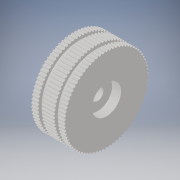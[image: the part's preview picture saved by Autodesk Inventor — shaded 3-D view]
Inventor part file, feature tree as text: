
AUTODESK INVENTOR PART (.ipt)
format: ipt  version: 2019 (Build 230136000, 136)  size: 681,984 bytes
history: native  units: in
note: dims shown in document units (in); Inventor stores cm internally (conversion verified against a paired STEP export)
features: sketch x7, extrude x6, revolve x1, projected_geometry x1
ambient origin geometry x8: Origin, YZ Plane, XZ Plane, XY Plane, X Axis, Y Axis, Z Axis, Center Point
bodies: Solid1 (feature_tree)
feature tree (15):
  extrude  "Extrusion1"  Depth=1.0in TaperAngle=0.0deg
  extrude  "Extrusion2"  Depth=0.27in TaperAngle=0.0deg
  extrude  "Extrusion3"  Depth=0.27in TaperAngle=0.0deg
  extrude  "Extrusion8"  Depth=0.3937in TaperAngle=0.0deg
  extrude  "Extrusion10"  Depth=1.0in TaperAngle=0.0deg
  extrude  "Extrusion11"  Depth=31.4961in TaperAngle=360.0deg
  revolve  "Revolution2"  [1 undecoded]
  sketch  "Sketch1"  dims[d3=0.35in d4=1.0in d5=0.0in]
  sketch  "Sketch2"  dims[d6=0.865in d7=0.27in d8=0.0in]
  sketch  "Sketch3"  dims[d9=0.865in d10=0.27in d11=0.0in]
  sketch  "Sketch5"  dims[d48=0.88in d49=0.3937in d50=0.0in]
  sketch  "Sketch8"  dims[d54=2.5591in d55=1.0in d56=0.0in]
  projected_geometry  "Projected Loop1"
  sketch  "Sketch9"  dims[d57=0.0787in d58=31.4961in d60=360.0deg]
  sketch  "Sketch10"  dims[d62=1.0187in d63=0.0in d64=0.1181in d65=0.1181in d66=0.1969in d67=0.1969in d68=0.1181in d70=90.0deg]
note: 1 required parameter value undecoded (feature->parameter linkage not recoverable at this tier; creation-order binding heuristic only, values carry confidence <= 0.55)
